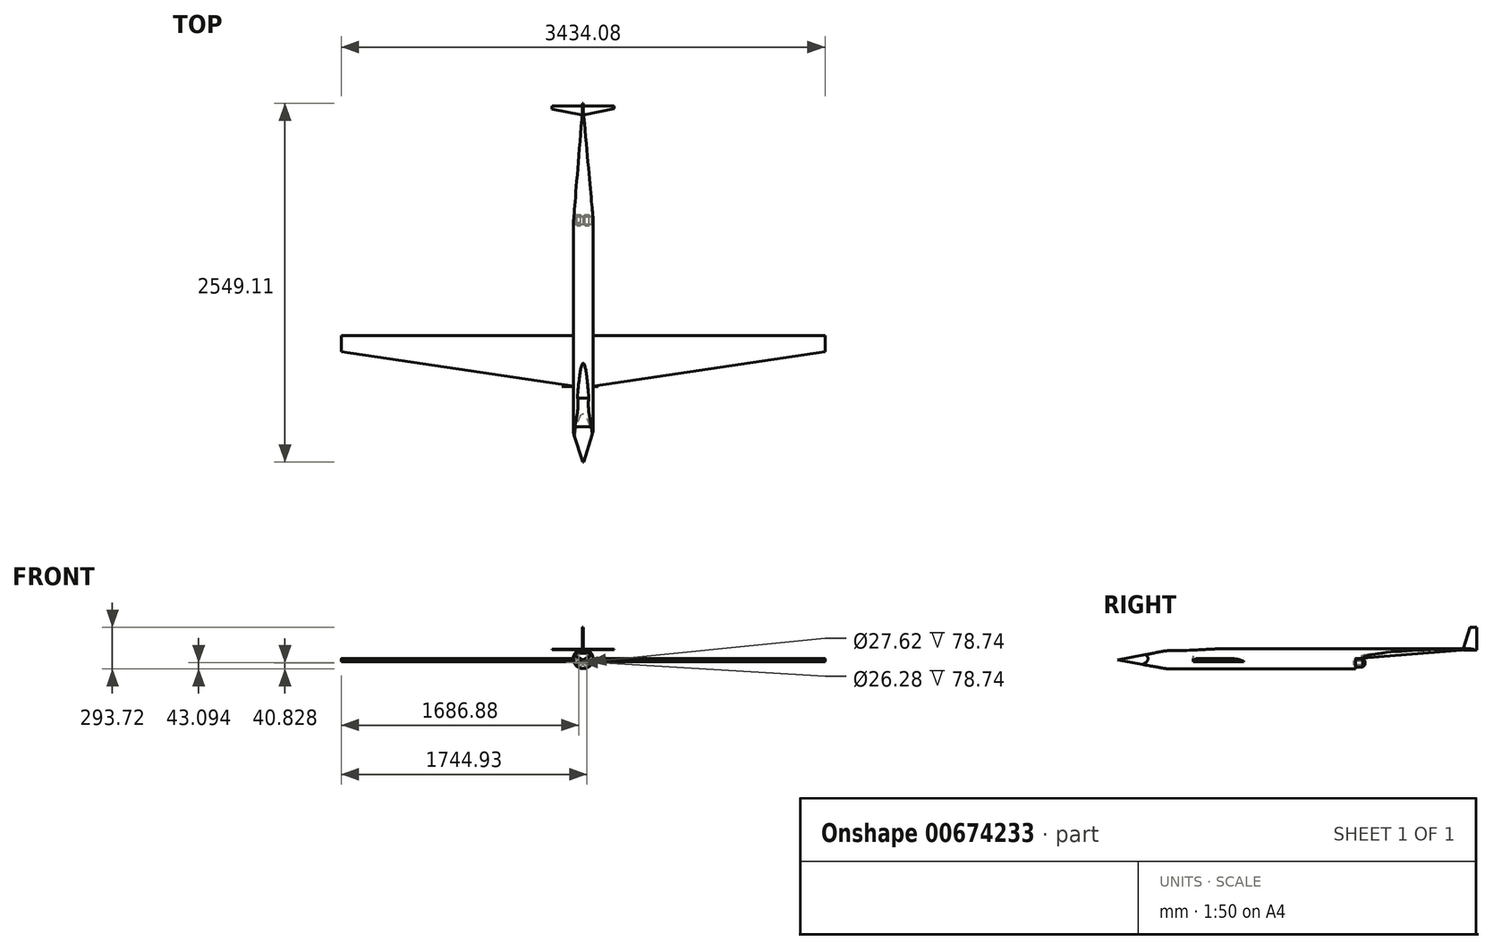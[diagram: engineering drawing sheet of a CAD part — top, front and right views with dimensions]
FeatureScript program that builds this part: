
annotation { "Feature Type Name" : "Feature", "Feature Type Description" : "" }
export const myFeature = defineFeature(function(context is Context, id is Id, definition is map)
    precondition{}
    {
        {
            var Q0;
            Q0=qCreatedBy(makeId("Front.planeOp"),FACE);
            var sketch = newSketch(context, id + "F0", { "sketchPlane" : qUnion([Q0])});
            skCircle(sketch, "E0", {"center": v(0, 0) * mm, "radius": 70.2 * mm});
            skSolve(sketch);
        }
        {
            var Q0;
            Q0 = qSketchRegion(id + "F0", true);
            extrude(context, id + "F1", {"entities" : qUnion([Q0]), "endBound" : BoundingType.SYMMETRIC, "depth" : 2540 * mm, "offsetDistance" : 25.4 * mm});
        }
        {
            var Q0;
            Q0=qCreatedBy(makeId("Right.planeOp"),FACE);
            var sketch = newSketch(context, id + "F2", { "sketchPlane" : qUnion([Q0])});
            skLineSegment(sketch, "E1", {"start": v(422.3, -123.23) * mm, "end": v(422.3, 0) * mm});
            skLineSegment(sketch, "E2", {"start": v(422.3, 0) * mm, "end": v(1309.28, 72.24) * mm});
            skLineSegment(sketch, "E3", {"start": v(1309.28, 72.24) * mm, "end": v(1309.28, -93.8) * mm});
            skLineSegment(sketch, "E4", {"start": v(1309.28, -93.8) * mm, "end": v(422.3, -123.23) * mm});
            skSolve(sketch);
        }
        {
            var Q0;
            Q0 = qSketchRegion(id + "F2", true);
            extrude(context, id + "F3", {"entities" : qUnion([Q0]), "operationType" : NewBodyOperationType.REMOVE, "endBound" : BoundingType.SYMMETRIC, "oppositeDirection" : true, "depth" : 680.72 * mm, "offsetDistance" : 25.4 * mm});
        }
        {
            var Q0;
            Q0=qCreatedBy(makeId("Top.planeOp"),FACE);
            var sketch = newSketch(context, id + "F4", { "sketchPlane" : qUnion([Q0])});
            skLineSegment(sketch, "E5", {"start": v(-70.04, 419.84) * mm, "end": v(0, 1291.04) * mm});
            skLineSegment(sketch, "E6", {"start": v(-2.07, 1265.3) * mm, "end": v(74.56, 420.68) * mm});
            skLineSegment(sketch, "E7", {"start": v(74.56, 420.68) * mm, "end": v(380.8, 1336.03) * mm});
            skLineSegment(sketch, "E8", {"start": v(380.8, 1336.03) * mm, "end": v(-325.15, 1336.03) * mm});
            skLineSegment(sketch, "E9", {"start": v(-325.15, 1336.03) * mm, "end": v(-70.04, 419.84) * mm});
            skSolve(sketch);
        }
        {
            var Q0;
            Q0 = qSketchRegion(id + "F4", true);
            extrude(context, id + "F5", {"entities" : qUnion([Q0]), "operationType" : NewBodyOperationType.REMOVE, "endBound" : BoundingType.SYMMETRIC, "oppositeDirection" : true, "depth" : 2148.84 * mm, "offsetDistance" : 25.4 * mm});
        }
        {
            var Q0;
            Q0=qCreatedBy(makeId("Front.planeOp"),FACE);
            var sketch = newSketch(context, id + "F6", { "sketchPlane" : qUnion([Q0])});
            skCircle(sketch, "E10", {"center": v(27.9, -29.37) * mm, "radius": 29.05 * mm});
            skCircle(sketch, "E11", {"center": v(-30.16, -27.1) * mm, "radius": 28.38 * mm});
            skSolve(sketch);
        }
        {
            var Q0;
            Q0 = qSketchRegion(id + "F6", true);
            extrude(context, id + "F7", {"entities" : qUnion([Q0]), "operationType" : NewBodyOperationType.ADD, "oppositeDirection" : true, "depth" : 488.7 * mm, "offsetDistance" : 25.4 * mm});
        }
        {
            var Q0;
            Q0=makeQuery(id+"F7.opExtrude","CAP_EDGE",EDGE,{"disambiguationData":[OSD([sQuery(id+"F6.wireOp",EDGE,"E11")])],"isStart":false});
            var Q1;
            Q1=makeQuery(id+"F7.opExtrude","CAP_EDGE",EDGE,{"disambiguationData":[OSD([sQuery(id+"F6.wireOp",EDGE,"E10")])],"isStart":false});
            chamfer(context, id + "F8", {"entities" : qUnion([Q0, Q1]), "width" : 15.24 * mm, "tangentPropagation" : true});
        }
        {
            var Q0;
            Q0=makeQuery(id+"F7.opExtrude","CAP_FACE",FACE,{"disambiguationData":[OSD([sQuery(id+"F6.wireOp",EDGE,"E11")])],"isStart":false});
            var Q1;
            Q1=makeQuery(id+"F7.opExtrude","CAP_FACE",FACE,{"disambiguationData":[OSD([sQuery(id+"F6.wireOp",EDGE,"E10")])],"isStart":false});
            extrude(context, id + "F9", {"entities" : qUnion([Q0, Q1]), "operationType" : NewBodyOperationType.REMOVE, "oppositeDirection" : true, "depth" : 78.74 * mm, "offsetDistance" : 25.4 * mm});
        }
        {
            var Q0;
            Q0=qCreatedBy(makeId("Right.planeOp"),FACE);
            var sketch = newSketch(context, id + "F10", { "sketchPlane" : qUnion([Q0])});
            skLineSegment(sketch, "E12", {"start": v(-1267.96, -9.44) * mm, "end": v(-1017.25, 38.77) * mm});
            skLineSegment(sketch, "E13", {"start": v(-1267.96, -9.44) * mm, "end": v(-865.93, -80.65) * mm});
            skFitSpline(sketch, "E14", {"points": [v(-1017.25, 38.77) * mm, v(-904.5, 58.06) * mm, v(-814.75, 58.06) * mm, v(-813.27, 57.32) * mm], "startDerivative": vector(209.73, 48.52) * mm, "endDerivative": vector(13.16, -12.58) * mm});
            skLineSegment(sketch, "E15", {"start": v(-813.27, 57.32) * mm, "end": v(-487.63, 74.28) * mm});
            skLineSegment(sketch, "E16", {"start": v(-487.63, 74.28) * mm, "end": v(-1744.98, 174.35) * mm});
            skLineSegment(sketch, "E17", {"start": v(-1744.98, 174.35) * mm, "end": v(-1656.24, -127.8) * mm});
            skLineSegment(sketch, "E18", {"start": v(-1656.24, -127.8) * mm, "end": v(-865.93, -80.65) * mm});
            skSolve(sketch);
        }
        {
            var Q0;
            Q0 = qSketchRegion(id + "F10", true);
            extrude(context, id + "F11", {"entities" : qUnion([Q0]), "operationType" : NewBodyOperationType.REMOVE, "endBound" : BoundingType.SYMMETRIC, "oppositeDirection" : true, "depth" : 894.08 * mm, "offsetDistance" : 25.4 * mm});
        }
        {
            var Q0;
            Q0=qCreatedBy(makeId("Top.planeOp"),FACE);
            var sketch = newSketch(context, id + "F12", { "sketchPlane" : qUnion([Q0])});
            skLineSegment(sketch, "E19", {"start": v(-121.62, -894.06) * mm, "end": v(0, -1278.26) * mm});
            skLineSegment(sketch, "E20", {"start": v(0, -1278.26) * mm, "end": v(119.58, -891.48) * mm});
            skLineSegment(sketch, "E21", {"start": v(119.58, -891.48) * mm, "end": v(74.79, -1506.55) * mm});
            skLineSegment(sketch, "E22", {"start": v(74.79, -1506.55) * mm, "end": v(-197.43, -1130.1) * mm});
            skLineSegment(sketch, "E23", {"start": v(-197.43, -1130.1) * mm, "end": v(-121.62, -894.06) * mm});
            skSolve(sketch);
        }
        {
            var Q0;
            Q0 = qSketchRegion(id + "F12", true);
            extrude(context, id + "F13", {"entities" : qUnion([Q0]), "operationType" : NewBodyOperationType.REMOVE, "endBound" : BoundingType.SYMMETRIC, "oppositeDirection" : true, "depth" : 828.04 * mm, "offsetDistance" : 25.4 * mm});
        }
        {
            var Q0;
            Q0=qCreatedBy(makeId("Right.planeOp"),FACE);
            var sketch = newSketch(context, id + "F14", { "sketchPlane" : qUnion([Q0])});
            skLineSegment(sketch, "E24.bottom", {"start": v(-730.82, 0) * mm, "end": v(-370.5, 0) * mm});
            skLineSegment(sketch, "E24.top", {"start": v(-730.82, -20.2) * mm, "end": v(-370.5, -20.2) * mm});
            skLineSegment(sketch, "E24.left", {"start": v(-730.82, 0) * mm, "end": v(-730.82, -20.2) * mm});
            skLineSegment(sketch, "E24.right", {"start": v(-370.5, 0) * mm, "end": v(-370.5, -20.2) * mm});
            skSolve(sketch);
        }
        {
            var Q0;
            Q0 = qSketchRegion(id + "F14", true);
            extrude(context, id + "F15", {"entities" : qUnion([Q0]), "operationType" : NewBodyOperationType.ADD, "endBound" : BoundingType.SYMMETRIC, "depth" : 3434.08 * mm, "offsetDistance" : 25.4 * mm});
        }
        {
            var Q0;
            Q0=qCreatedBy(makeId("Top.planeOp"),FACE);
            var sketch = newSketch(context, id + "F16", { "sketchPlane" : qUnion([Q0])});
            skLineSegment(sketch, "E25", {"start": v(-67.59, -729.58) * mm, "end": v(-1733.62, -482.88) * mm});
            skLineSegment(sketch, "E26", {"start": v(-1733.62, -482.88) * mm, "end": v(-1773.93, -755.15) * mm});
            skLineSegment(sketch, "E27", {"start": v(-1773.93, -755.15) * mm, "end": v(-67.59, -729.58) * mm});
            skLineSegment(sketch, "E28", {"start": v(77.73, -729.58) * mm, "end": v(1720.1, -482.88) * mm});
            skLineSegment(sketch, "E29", {"start": v(1720.1, -482.88) * mm, "end": v(1768.15, -802.8) * mm});
            skLineSegment(sketch, "E30", {"start": v(1768.15, -802.8) * mm, "end": v(77.73, -729.58) * mm});
            skSolve(sketch);
        }
        {
            var Q0;
            Q0 = qSketchRegion(id + "F16", true);
            extrude(context, id + "F17", {"entities" : qUnion([Q0]), "operationType" : NewBodyOperationType.REMOVE, "endBound" : BoundingType.SYMMETRIC, "oppositeDirection" : true, "depth" : 1310.64 * mm, "offsetDistance" : 25.4 * mm});
        }
        {
            var Q0;
            {var subQ0=sQuery(id+"F14.wireOp",EDGE,"E24.left");var subQ1=sQuery(id+"F14.wireOp",EDGE,"E24.right");var subQ2=sQuery(id+"F14.wireOp",EDGE,"E24.bottom");Q0=makeQuery(id+"F17.boolean.opBoolean","INTERSECT",EDGE,{"derivedFrom":[makeQuery(id+"F15.boolean.opBoolean","SPLIT",FACE,{"disambiguationData":[TD([makeQuery(id+"F15.opExtrude","CAP_FACE",FACE,{"disambiguationData":[OSD([subQ2,sQuery(id+"F14.wireOp",EDGE,"E24.top"),subQ0,subQ1])],"isStart":false})])],"derivedFrom":makeQuery(id+"F15.opExtrude","SWEPT_FACE",FACE,{"disambiguationData":[OSD([subQ2])]})}),makeQuery(id+"F17.opExtrude","SWEPT_FACE",FACE,{"disambiguationData":[OSD([sQuery(id+"F16.wireOp",EDGE,"E28")])]})]});}
            var Q1;
            {var subQ0=sQuery(id+"F14.wireOp",EDGE,"E24.left");var subQ1=sQuery(id+"F14.wireOp",EDGE,"E24.right");var subQ2=sQuery(id+"F14.wireOp",EDGE,"E24.bottom");Q1=makeQuery(id+"F17.boolean.opBoolean","INTERSECT",EDGE,{"derivedFrom":[makeQuery(id+"F15.boolean.opBoolean","SPLIT",FACE,{"disambiguationData":[TD([makeQuery(id+"F15.opExtrude","CAP_FACE",FACE,{"disambiguationData":[OSD([subQ2,sQuery(id+"F14.wireOp",EDGE,"E24.top"),subQ0,subQ1])],"isStart":true})])],"derivedFrom":makeQuery(id+"F15.opExtrude","SWEPT_FACE",FACE,{"disambiguationData":[OSD([subQ2])]})}),makeQuery(id+"F17.opExtrude","SWEPT_FACE",FACE,{"disambiguationData":[OSD([sQuery(id+"F16.wireOp",EDGE,"E25")])]})]});}
            fillet(context, id + "F18", {"entities" : qUnion([Q0, Q1]), "radius" : 26.37 * mm, "tangentPropagation" : true, "allowEdgeOverflow" : false});
        }
        {
            var Q0;
            {var subQ0=sQuery(id+"F14.wireOp",EDGE,"E24.bottom");var subQ1=sQuery(id+"F14.wireOp",EDGE,"E24.right");Q0=makeQuery(id+"F15.boolean.opBoolean","SPLIT",EDGE,{"disambiguationData":[TD([makeQuery(id+"F15.opExtrude","CAP_FACE",FACE,{"disambiguationData":[OSD([subQ0,sQuery(id+"F14.wireOp",EDGE,"E24.top"),sQuery(id+"F14.wireOp",EDGE,"E24.left"),subQ1])],"isStart":false})])],"derivedFrom":makeQuery(id+"F15.opExtrude","SWEPT_EDGE",EDGE,{"disambiguationData":[OSD([subQ0,subQ1])]})});}
            var Q1;
            {var subQ0=sQuery(id+"F14.wireOp",EDGE,"E24.bottom");var subQ1=sQuery(id+"F14.wireOp",EDGE,"E24.right");Q1=makeQuery(id+"F15.boolean.opBoolean","SPLIT",EDGE,{"disambiguationData":[TD([makeQuery(id+"F15.opExtrude","CAP_FACE",FACE,{"disambiguationData":[OSD([subQ0,sQuery(id+"F14.wireOp",EDGE,"E24.top"),sQuery(id+"F14.wireOp",EDGE,"E24.left"),subQ1])],"isStart":true})])],"derivedFrom":makeQuery(id+"F15.opExtrude","SWEPT_EDGE",EDGE,{"disambiguationData":[OSD([subQ0,subQ1])]})});}
            fillet(context, id + "F19", {"entities" : qUnion([Q0, Q1]), "radius" : 172.93 * mm, "tangentPropagation" : true, "allowEdgeOverflow" : false});
        }
        {
            var Q0;
            Q0=qCreatedBy(makeId("Right.planeOp"),FACE);
            var sketch = newSketch(context, id + "F20", { "sketchPlane" : qUnion([Q0])});
            skLineSegment(sketch, "E31.bottom", {"start": v(1196.46, 69.46) * mm, "end": v(1263.16, 69.46) * mm});
            skLineSegment(sketch, "E31.top", {"start": v(1196.46, 64.64) * mm, "end": v(1263.16, 64.64) * mm});
            skLineSegment(sketch, "E31.left", {"start": v(1196.46, 69.46) * mm, "end": v(1196.46, 64.64) * mm});
            skLineSegment(sketch, "E31.right", {"start": v(1263.16, 69.46) * mm, "end": v(1263.16, 64.64) * mm});
            skSolve(sketch);
        }
        {
            var Q0;
            Q0 = qSketchRegion(id + "F20", true);
            extrude(context, id + "F21", {"entities" : qUnion([Q0]), "operationType" : NewBodyOperationType.ADD, "endBound" : BoundingType.SYMMETRIC, "depth" : 441.96 * mm, "offsetDistance" : 25.4 * mm});
        }
        {
            var Q0;
            Q0=qCreatedBy(makeId("Top.planeOp"),FACE);
            var sketch = newSketch(context, id + "F22", { "sketchPlane" : qUnion([Q0])});
            skLineSegment(sketch, "E32.bottom", {"start": v(-5.5, 1187.22) * mm, "end": v(0, 1187.22) * mm});
            skLineSegment(sketch, "E32.top", {"start": v(-5.5, 1281.15) * mm, "end": v(0, 1281.15) * mm});
            skLineSegment(sketch, "E32.left", {"start": v(-5.5, 1187.22) * mm, "end": v(-5.5, 1281.15) * mm});
            skLineSegment(sketch, "E32.right", {"start": v(0, 1187.22) * mm, "end": v(0, 1281.15) * mm});
            skSolve(sketch);
        }
        {
            var Q0;
            Q0 = qSketchRegion(id + "F22", true);
            extrude(context, id + "F23", {"entities" : qUnion([Q0]), "operationType" : NewBodyOperationType.ADD, "depth" : 223.52 * mm, "offsetDistance" : 25.4 * mm});
        }
        {
            var Q0;
            Q0=qCreatedBy(makeId("Right.planeOp"),FACE);
            var sketch = newSketch(context, id + "F24", { "sketchPlane" : qUnion([Q0])});
            skLineSegment(sketch, "E33", {"start": v(1180.13, 60.27) * mm, "end": v(1336.23, 60.27) * mm});
            skLineSegment(sketch, "E34", {"start": v(1336.23, 60.27) * mm, "end": v(1247.54, -52.36) * mm});
            skLineSegment(sketch, "E35", {"start": v(1247.54, -52.36) * mm, "end": v(1077.25, 8.83) * mm});
            skLineSegment(sketch, "E36", {"start": v(1077.25, 8.83) * mm, "end": v(1180.13, 60.27) * mm});
            skSolve(sketch);
        }
        {
            var Q0;
            Q0 = qSketchRegion(id + "F24", true);
            extrude(context, id + "F25", {"entities" : qUnion([Q0]), "operationType" : NewBodyOperationType.REMOVE, "endBound" : BoundingType.SYMMETRIC, "oppositeDirection" : true, "depth" : 71.12 * mm, "offsetDistance" : 25.4 * mm});
        }
        {
            var Q0;
            Q0=qCreatedBy(makeId("Top.planeOp"),FACE);
            var sketch = newSketch(context, id + "F26", { "sketchPlane" : qUnion([Q0])});
            skLineSegment(sketch, "E37", {"start": v(-234.03, 1244.38) * mm, "end": v(-9.54, 1197.5) * mm});
            skLineSegment(sketch, "E38", {"start": v(-9.54, 1197.5) * mm, "end": v(-396.01, 1152.73) * mm});
            skLineSegment(sketch, "E39", {"start": v(-396.01, 1152.73) * mm, "end": v(-234.03, 1244.38) * mm});
            skLineSegment(sketch, "E40", {"start": v(5.38, 1197.5) * mm, "end": v(233.43, 1244.38) * mm});
            skLineSegment(sketch, "E41", {"start": v(233.43, 1244.38) * mm, "end": v(233.43, 1152.73) * mm});
            skLineSegment(sketch, "E42", {"start": v(233.43, 1152.73) * mm, "end": v(5.38, 1197.5) * mm});
            skSolve(sketch);
        }
        {
            var Q0;
            Q0 = qSketchRegion(id + "F26", true);
            extrude(context, id + "F27", {"entities" : qUnion([Q0]), "operationType" : NewBodyOperationType.REMOVE, "endBound" : BoundingType.SYMMETRIC, "depth" : 415.54 * mm, "offsetDistance" : 25.4 * mm});
        }
        {
            var Q0;
            Q0=qCreatedBy(makeId("Right.planeOp"),FACE);
            var sketch = newSketch(context, id + "F28", { "sketchPlane" : qUnion([Q0])});
            skLineSegment(sketch, "E43", {"start": v(1186.7, 69.93) * mm, "end": v(1240.49, 240.79) * mm});
            skLineSegment(sketch, "E44", {"start": v(1240.49, 240.79) * mm, "end": v(1113.92, 215.47) * mm});
            skLineSegment(sketch, "E45", {"start": v(1113.92, 215.47) * mm, "end": v(1186.7, 69.93) * mm});
            skSolve(sketch);
        }
        {
            var Q0;
            Q0 = qSketchRegion(id + "F28", true);
            extrude(context, id + "F29", {"entities" : qUnion([Q0]), "operationType" : NewBodyOperationType.REMOVE, "endBound" : BoundingType.SYMMETRIC, "oppositeDirection" : true, "depth" : 121.92 * mm, "offsetDistance" : 25.4 * mm});
        }
        {
            var Q0;
            Q0=makeQuery(id+"F29.boolean.opBoolean","INTERSECT",EDGE,{"derivedFrom":[makeQuery(id+"F23.opExtrude","SWEPT_FACE",FACE,{"disambiguationData":[OSD([sQuery(id+"F22.wireOp",EDGE,"E32.right")])]}),makeQuery(id+"F29.opExtrude","SWEPT_FACE",FACE,{"disambiguationData":[OSD([sQuery(id+"F28.wireOp",EDGE,"E43")])]})]});
            var Q1;
            Q1=makeQuery(id+"F29.boolean.opBoolean","INTERSECT",EDGE,{"derivedFrom":[makeQuery(id+"F23.opExtrude","SWEPT_FACE",FACE,{"disambiguationData":[OSD([sQuery(id+"F22.wireOp",EDGE,"E32.left")])]}),makeQuery(id+"F29.opExtrude","SWEPT_FACE",FACE,{"disambiguationData":[OSD([sQuery(id+"F28.wireOp",EDGE,"E43")])]})]});
            fillet(context, id + "F30", {"entities" : qUnion([Q0, Q1]), "radius" : 3.07 * mm, "tangentPropagation" : true, "allowEdgeOverflow" : false});
        }
    });
